# Revit family: Storage-Teknion-AFTT_A.V_Cart_Top-R2023
name_source: partatom
category: Furniture
units: mm (PartAtom-declared; Revit-internal decimal feet)

## family parameters
Always vertical = Yes
Cut with Voids When Loaded = No
Enable Cutting in Views = No
OmniClass Number = 23.40.20.00
OmniClass Title = General Furniture and Specialties
Render Appearance Source = Family Geometry
Room Calculation Point = No
Shared = Yes
Work Plane-Based = No

## types (2) — shared parameters
Assembly Code = E2020200
Manufacturer = Teknion
Manufacturer Fax = 416.661.4586
Part Number = AFTT
Product Documentation Link = https://www.teknion.com
Product Line = Storage
Product Page URL = https://www.teknion.com
Series = Tables & Collaborative Spaces
Sustainability Data = https://www.teknion.com
URL = www.teknion.com
Unit Weight URL = http://www.teknion.com
Warranty = http://www.teknion.com
zero-valued in all types: Default Elevation

## per-type parameters (varying)
| type | Cut-Out - Top | Description | Model | With Arm |
| With Arm | 3.5 " | A.V. Cart Top, With Arm, 32" Width | AFTT132 | Yes |
| Without Arm | 0.3 " | A.V. Cart Top, Without Arm, 32" Width | AFTT232 | No |

type visibility flags (boolean, named after types; folded from table):
- With Arm: Yes: (none)
- Without Arm: Yes: Without Arm

## geometry (parser evidence)
native form markers: Sweep x3
no freeform markers — native parametric forms only
